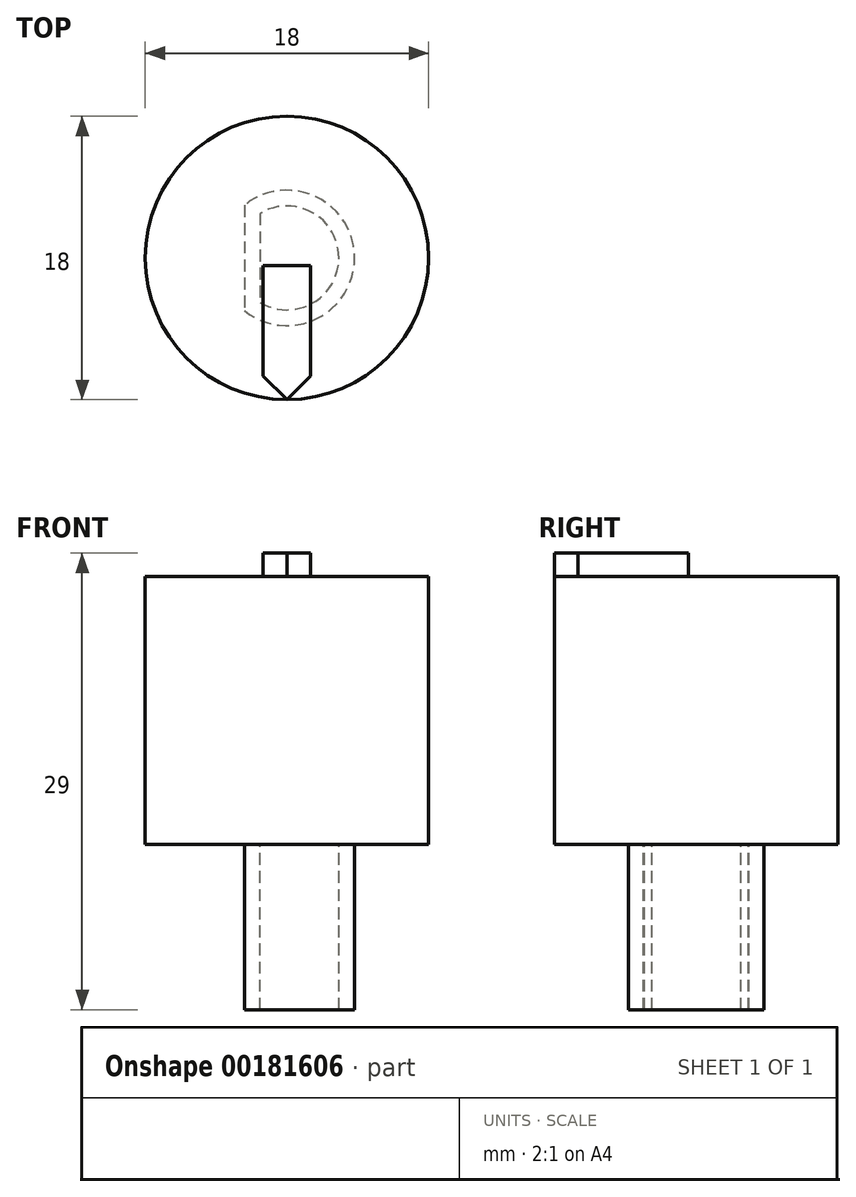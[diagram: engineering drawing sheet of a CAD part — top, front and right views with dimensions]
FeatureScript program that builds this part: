
annotation { "Feature Type Name" : "Feature", "Feature Type Description" : "" }
export const myFeature = defineFeature(function(context is Context, id is Id, definition is map)
    precondition{}
    {
        {
            var Q0;
            Q0=qCreatedBy(makeId("Top.planeOp"),FACE);
            var sketch = newSketch(context, id + "F0", { "sketchPlane" : qUnion([Q0])});
            skCircle(sketch, "E0", {"center": v(0, 0) * mm, "radius": 9 * mm});
            skCircle(sketch, "E1", {"center": v(0, 0) * mm, "radius": 4.3 * mm});
            skLineSegment(sketch, "E2", {"start": v(-2.7, 3.35) * mm, "end": v(-2.7, -3.35) * mm});
            skArc(sketch, "E3", {"start": v(-1.7, 2.83) * mm, "mid": v(3.3, 0) * mm, "end": v(-1.7, -2.83) * mm});
            skLineSegment(sketch, "E4", {"start": v(-1.7, 2.83) * mm, "end": v(-1.7, -2.83) * mm});
            skSolve(sketch);
        }
        {
            var Q0;
            {var subQ0=sQuery(id+"F0.wireOp",EDGE,"E4");Q0=makeQuery(id+"F0.imprint","IMPRINT",FACE,{"disambiguationData":[TD([[makeQuery(id+"F0.imprint","IMPRINT",EDGE,{"derivedFrom":subQ0}),1.0]])]});}
            var Q1;
            {var subQ0=sQuery(id+"F0.wireOp",EDGE,"E2");Q1=makeQuery(id+"F0.imprint","IMPRINT",FACE,{"disambiguationData":[TD([[makeQuery(id+"F0.imprint","IMPRINT",EDGE,{"derivedFrom":subQ0}),-1.0]])]});}
            var Q2;
            {var subQ4=sQuery(id+"F0.wireOp",EDGE,"E2");Q2=makeQuery(id+"F0.imprint","IMPRINT",FACE,{"disambiguationData":[TD([[makeQuery(id+"F0.imprint","IMPRINT",EDGE,{"derivedFrom":subQ4}),1.0]])]});}
            var Q3;
            Q3=makeQuery(id+"F0.imprint","IMPRINT",FACE,{"disambiguationData":[TD([[makeQuery(id+"F0.imprint","IMPRINT",EDGE,{"derivedFrom":sQuery(id+"F0.wireOp",EDGE,"E0")}),1.0]])]});
            var Q4;
            {var subQ0=sQuery(id+"F0.wireOp",EDGE,"FSIPDkNn-DrQF-lx5f-XINl-FDNYDJzQY5bG");var subQ1=sQuery(id+"F0.wireOp",EDGE,"E3");var subQ2=makeQuery(id+"F0.imprint","INTERSECT",VERTEX,{"disambiguationData":[OD(0.0)],"derivedFrom":[subQ1,subQ0]});Q4=makeQuery(id+"F0.imprint","IMPRINT",FACE,{"disambiguationData":[TD([[makeQuery(id+"F0.imprint","IMPRINT",EDGE,{"disambiguationData":[TD([[subQ2,-1.0]])],"derivedFrom":subQ1}),-1.0]])]});}
            var Q5;
            {var subQ1=sQuery(id+"F0.wireOp",EDGE,"jtoO9AOW-OG8r-op2T-0eIV-xee9z17cBor1");var subQ3=sQuery(id+"F0.wireOp",EDGE,"E1");var subQ4=makeQuery(id+"F0.imprint","INTERSECT",VERTEX,{"derivedFrom":[subQ3,subQ1]});Q5=makeQuery(id+"F0.imprint","IMPRINT",FACE,{"disambiguationData":[TD([[makeQuery(id+"F0.imprint","IMPRINT",EDGE,{"disambiguationData":[TD([[subQ4,-1.0]])],"derivedFrom":subQ3}),1.0]])]});}
            var Q6;
            {var subQ2=sQuery(id+"F0.wireOp",EDGE,"a9V57k9W-iK3Q-zI9n-wZaT-DJcMQNuYsHNN");Q6=makeQuery(id+"F0.imprint","IMPRINT",FACE,{"disambiguationData":[TD([[makeQuery(id+"F0.imprint","IMPRINT",EDGE,{"derivedFrom":subQ2}),1.0]])]});}
            extrude(context, id + "F1", {"entities" : qUnion([Q0, Q1, Q2, Q3, Q4, Q5, Q6]), "depth" : 17 * mm});
        }
        {
            var Q0;
            {var subQ0=sQuery(id+"F0.wireOp",EDGE,"E2");Q0=makeQuery(id+"F0.imprint","IMPRINT",FACE,{"disambiguationData":[TD([[makeQuery(id+"F0.imprint","IMPRINT",EDGE,{"derivedFrom":subQ0}),1.0]])]});}
            var Q1;
            {var subQ5=sQuery(id+"F0.wireOp",EDGE,"FSIPDkNn-DrQF-lx5f-XINl-FDNYDJzQY5bG");Q1=makeQuery(id+"F0.imprint","IMPRINT",FACE,{"disambiguationData":[TD([[makeQuery(id+"F0.imprint","IMPRINT",EDGE,{"derivedFrom":subQ5}),-1.0]])]});}
            extrude(context, id + "F2", {"entities" : qUnion([Q0, Q1]), "operationType" : NewBodyOperationType.ADD, "oppositeDirection" : true, "depth" : 10.5 * mm});
        }
        {
            var Q0;
            Q0=makeQuery(id+"F1.opExtrude","CAP_FACE",FACE,{"disambiguationData":[OSD([sQuery(id+"F0.wireOp",EDGE,"E0")])],"isStart":false});
            var sketch = newSketch(context, id + "F3", { "sketchPlane" : qUnion([Q0])});
            skLineSegment(sketch, "E5", {"start": v(0, -9) * mm, "end": v(1.5, -7.5) * mm});
            skLineSegment(sketch, "E6", {"start": v(0, -9) * mm, "end": v(-1.5, -7.5) * mm});
            skLineSegment(sketch, "E7", {"start": v(-1.5, -7.5) * mm, "end": v(-1.5, -0.5) * mm});
            skLineSegment(sketch, "E8", {"start": v(1.5, -7.5) * mm, "end": v(1.5, -0.5) * mm});
            skLineSegment(sketch, "E9", {"start": v(1.5, -0.5) * mm, "end": v(-1.5, -0.5) * mm});
            skSolve(sketch);
        }
        {
            var Q0;
            Q0=makeQuery(id+"F3.imprint","IMPRINT",FACE,{"disambiguationData":[TD([[makeQuery(id+"F3.imprint","IMPRINT",EDGE,{"derivedFrom":sQuery(id+"F3.wireOp",EDGE,"E5")}),1.0]])]});
            extrude(context, id + "F4", {"entities" : qUnion([Q0]), "operationType" : NewBodyOperationType.ADD, "depth" : 1.5 * mm});
        }
    });
